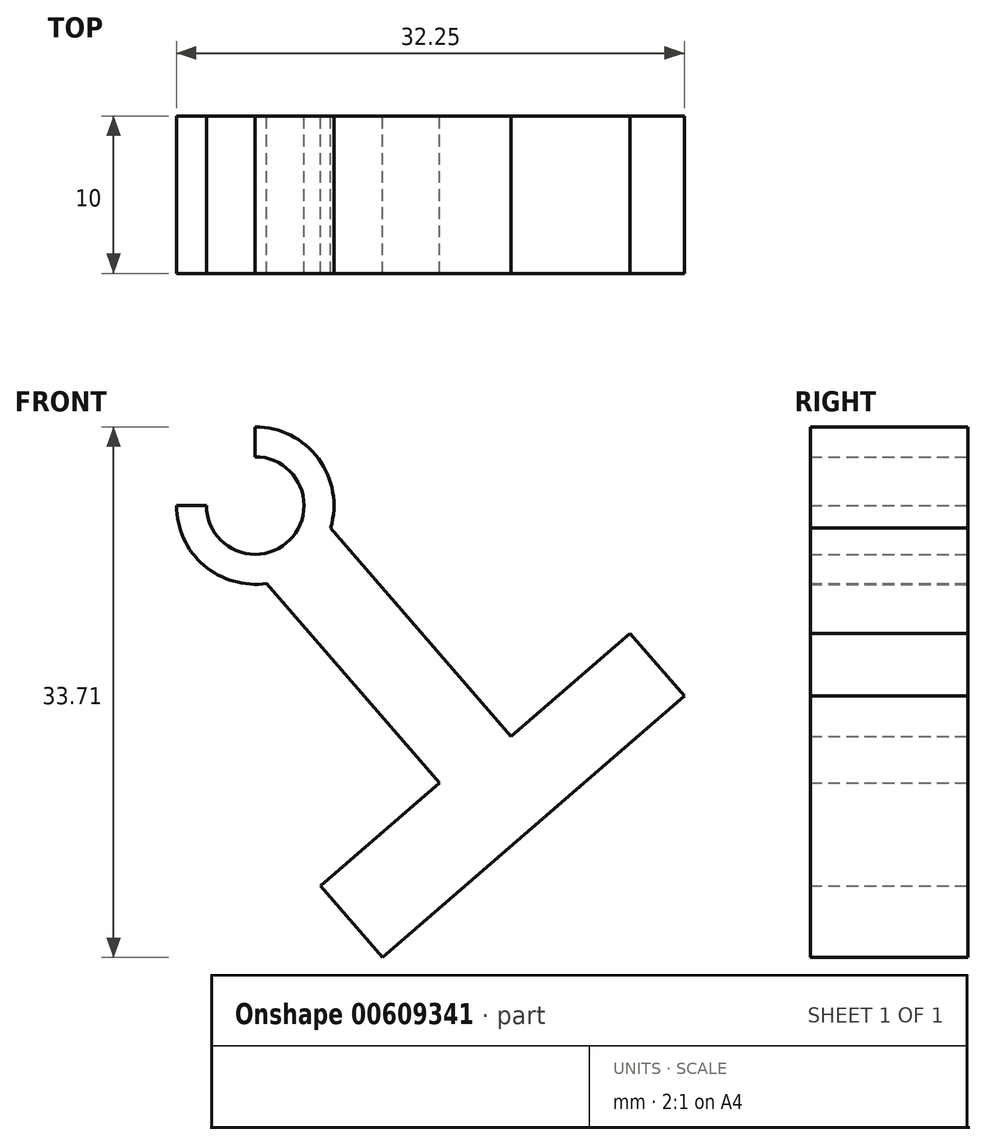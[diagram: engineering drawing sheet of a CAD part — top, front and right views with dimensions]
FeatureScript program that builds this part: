
annotation { "Feature Type Name" : "Feature", "Feature Type Description" : "" }
export const myFeature = defineFeature(function(context is Context, id is Id, definition is map)
    precondition{}
    {
        {
            var Q0;
            Q0=qCreatedBy(makeId("Front.planeOp"),FACE);
            var sketch = newSketch(context, id + "F0", { "sketchPlane" : qUnion([Q0])});
            skArc(sketch, "E0", {"start": v(-3.1, 0) * mm, "mid": v(2.2, -2.2) * mm, "end": v(0, 3.1) * mm});
            skLineSegment(sketch, "E1", {"start": v(0, 3.1) * mm, "end": v(0, 4.1) * mm});
            skLineSegment(sketch, "E2", {"start": v(-4.1, 0) * mm, "end": v(-3.1, 0) * mm});
            skLineSegment(sketch, "E3", {"start": v(2.2, -2.2) * mm, "end": v(2.2, -2.2) * mm, "construction": true});
            skLineSegment(sketch, "E4", {"start": v(2.03, -2.34) * mm, "end": v(2.2, -2.2) * mm});
            skLineSegment(sketch, "E5", {"start": v(4.79, -1.43) * mm, "end": v(16.25, -14.67) * mm});
            skLineSegment(sketch, "E6", {"start": v(11.7, -17.63) * mm, "end": v(0.73, -4.95) * mm});
            skLineSegment(sketch, "E7", {"start": v(11.7, -17.63) * mm, "end": v(4.15, -24.17) * mm});
            skLineSegment(sketch, "E8", {"start": v(4.15, -24.17) * mm, "end": v(8.07, -28.7) * mm});
            skLineSegment(sketch, "E9", {"start": v(8.07, -28.7) * mm, "end": v(27.25, -12.1) * mm});
            skLineSegment(sketch, "E10", {"start": v(27.25, -12.1) * mm, "end": v(23.8, -8.13) * mm});
            skLineSegment(sketch, "E11", {"start": v(23.8, -8.13) * mm, "end": v(16.25, -14.67) * mm});
            skArc(sketch, "E12", {"start": v(-5, 0) * mm, "mid": v(-3.27, -3.79) * mm, "end": v(0.73, -4.95) * mm});
            skLineSegment(sketch, "E13", {"start": v(0, 3.1) * mm, "end": v(0, 5) * mm});
            skLineSegment(sketch, "E14", {"start": v(-3.1, 0) * mm, "end": v(-5, 0) * mm});
            skPoint(sketch, "E15.end.orphan", {"position": v(0, -4.1) * mm});
            skArc(sketch, "E16.trimOffspring", {"start": v(4.79, -1.43) * mm, "mid": v(4.01, 2.99) * mm, "end": v(0, 5) * mm});
            skSolve(sketch);
        }
        {
            var Q0;
            Q0 = qSketchRegion(id + "F0", true);
            extrude(context, id + "F1", {"entities" : qUnion([Q0]), "depth" : 10 * mm, "offsetDistance" : 25 * mm});
        }
    });
